# Revit family: IS_TonicII_Multiproduct_BIM_DE_A6326;A6327
name_source: partatom
category: Plumbing Fixtures
revit_build: Autodesk Revit 2015 (Build: 20140606_1530(x64)
units: mm (PartAtom-declared; Revit-internal decimal feet)

## types (2) — shared parameters
A6326AA = Yes
AreaUnits = millimeters
Assembly Code = C1030200
AssetType = Fixed
BarCode = 4015413334938
Brand = Ideal Standard
ConnectionType = Plumbing
Default Elevation = 1219 mm
Description = A6326AA TONIC II single lever one hole basin mixer with pop-up waste
DurationUnit = year
ExpectedLife = 25
FaucetFunction = MIXED
FaucetOperation = Other
FaucetTopDescription = Lever
FaucetType = Other
Features = TONIC II single lever one hole basin mixer with pop-up waste
Finish = Chrome
IfcExportAs = IfcValveType
IfcExportType = FAUCET
InstallationDate = 1900-12-31T23:59:59
InstallationInstructions = www.idealstandard.de\produkte
LinearUnits = millimeters
ManufacturerURL = www.idealstandard.com
Model = A6326AA
ModelNumber = A6326AA
ModelReference = Tonic ii single lever basin mixer with pop-up waste
NBSDescription = Water supply fitting for wash basins and troughs
NBSReference = 45-35-70/371
NettWeight = 1.8 Kg
NominalHeight = 155 mm
NominalWidth = 51 mm
ProductInformation = www.idealstandard.de/produkte
Shape = Sculptured
Space = Internal
SpareParts = www.idealstandard.de/ersatzteile
TestPressure = 10 Bar
URL = www.idealstandard.com
Uniclass2015Code = Pr_40_20_87_98
Uniclass2015Title = Water supply fittings for wash basins and troughs
Uniclass2015Version = Products v1.1
Version = 1
VolumeUnits = Litres
WarrantyStartDate = 1900-12-31T23:59:59
WorkingPressure = 1-5 Bar

## per-type parameters (varying)
| type | BIMObjectName | Name | NominalDepth | NominalLength | Size |
| A6326AA - | ISI_IdealStandard_WashBasinTaps_TonicII_A6326 | WashBasinTaps_TonicII_A6326_IdealStandard | 0 mm  [stored 0 ft] | 0 mm  [stored 0 ft] | 155 x 0 x 51 mm |
| A6327AA - | ISI_IdealStandard_WashBasinTaps_TonicII_A6327 | WashBasinTaps_TonicII_A6327_IdealStandard | 145 mm  [stored 0.475722 ft] | 145 mm  [stored 0.475722 ft] | 155 x 145 x 51 mm |

note: [stored X ft] marks values corroborated as IEEE doubles in the binary element streams (Revit-internal decimal feet)

## geometry (parser evidence)
native form markers: Blend x2, Sweep x4
no freeform markers — native parametric forms only
